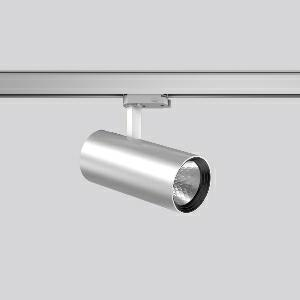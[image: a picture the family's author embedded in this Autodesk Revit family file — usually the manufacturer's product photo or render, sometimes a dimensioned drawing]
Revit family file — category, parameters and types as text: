
# Revit family: deecos_s_mini_742204_004_2_76_5e90
name_source: partatom
category: Lighting Fixtures
units: mm (PartAtom-declared; Revit-internal decimal feet)

## family parameters
Cut with Voids When Loaded = No
Host = Face
Light Source = No
Part Type = Normal
Room Calculation Point = No
Round Connector Dimension = Use Diameter
Shared = No

## types (1)
- DEECOS S mini (1 x LED Modul 927, 3300 lm, 2700)
    Apparent Load = 29 VA
    Approval mark = CE
    CIE Flux Codes = 99 100 100 100 100
    Color Rendering = 92
    Color Temperature = 2700
    Default Elevation = 1800 mm
    Description = Series: DEECOS S mini
LED surface-mounted projector in modern design with no visible cooling ribs. Housing: die-cast aluminium, powder-coated. Rotation range: 356°. Swivel range: 90°. Black plastic ring and recessed LED to prevent glare from the side. Optical assembly with reflector made of MIRO-Silver with 98% total light reflection for outstanding efficiency - can be changed without tools. Best colour rendering index Ra>90. With adapter for RZB 3-circuit DALI tracks. Suitable for Track on ceiling, Wall track. High quality converter without flickering and stroboscopic effect. The following accessories can be mounted without use of tools: interchangeable lenses, decorative glasses, honeycomb louvre, clear and frosted diffusers, white interchangeable plastic ring. 
Colour: silver
Diameter: 87 mm
Height: 214 mm
Lamp: LED
Socket: without socket
Colour temperature: 2700K
Colour rendering index (CRI): 92
System power: 29 W
Rated luminous flux: 3300 lm
Luminous efficiency: 114 lm/W
Control gear: Converter, dimmable, DALI
Protection class: I
Type of protection: IP 20
    Height = 214 mm
    Lamp = 1 x LED Modul 927
    Lamp Light Flux = 3300 lm
    Lamp count = 1
    Length = 87 mm
    Lifetime = 50000 h
    Luminous efficacy = 114 lm/W
    Manufacturer = RZB
    ModVariant = No
    Model = 742204.004.2.76
    Mounting Place = Ceiling
    Mounting Type = Rail mounted
    Number of Poles = 1
    OnlyDefault = Yes
    Power Factor = 1
    Product Name = DEECOS S mini
    Product group = Track mounted projectors
    ProductGroupID = 301
    Protection Class = Protection class I
    Protection Degree = IP 20
    RLX_Detail_Level = 1
    RLX_Emergency_Light_Flux = 0 lm
    RLX_Emergency_Type = 0
    RLX_Emergency_Type_DB = No
    RlxData = <blob elided: 37129 chars, md5=853b5b7b>
    Socket = socket
    Standby Power = 0 W
    System Light Flux = 3300 lm
    System Power = 29 W
    Type Comments = Product without accessories
    Type Image = 741926.004.jpg
    URL = http://relux.com
    VarID = ---
    Voltage = 230 V
    Voltage Range = 220-240 V
    Weight = 0.00 kg
    Width = 0 mm  [stored 0 ft]

note: [stored X ft] marks values corroborated as IEEE doubles in the binary element streams (Revit-internal decimal feet)

## geometry (parser evidence)
native form markers: Blend x4, Sweep x13
no freeform markers — native parametric forms only
